# Revit family: Door-NanaWall-Acoustic-645_UPDATED_v2
name_source: partatom
category: Doors
units: mm (PartAtom-declared; Revit-internal decimal feet)

## family parameters
Always vertical = Yes
Cut with Voids When Loaded = No
Host = Wall
OmniClass Number = 23.30.10.17.17
OmniClass Title = Folding Doors and Grilles
Room Calculation Point = No
Shared = No

## types (3) — shared parameters
04 CSI = 08 41 13
95 CSI = 8411
Analytic Construction = <None>
Assembly Code = B2050.4010
Cost Info = https://www.nanawall.com
Description = Acoustical  floor supported folding glass wall
Disclaimer = Please note that the Revit model is for schematic purposes only.  To obtain a detailed 3D model, please go to the NanaWall's configurator at www.nanawall.com.
Engineering Details URL = https://www.nanawall.com
Filler = Rubber - NanaWall - Black
Glass Material = Glass - NanaWall - Generic
Installation and Service URL = http://www.nanawall.com
Keynote = 08 14 73
Manufacturer = NanaWall Systems, Inc.
Manufacturer Fax = (415) 383-0312
Model = NW Acoustical 645
Performance URL = https://www.nanawall.com
Product Page URL = https://www.nanawall.com
Sash = Metal - NanaWall - Aluminum
Sill = Metal - NanaWall - Aluminum
Sills Available = Flush Sill, Minimal Interior Sill
Subcategory = Folding Door
Thickness = 67.2 mm  [stored 0.220472 ft]
U Value = 0.27
URL = http://www.nanawall.com
Wall Closure = By host
Warranty URL = http://www.nanawall.com
c Hinge Offset = 33.6 mm
c Top Frame Lat Offset = 55.5 mm

## per-type parameters (varying)
| type | Constraints | c Down Offset |
| Standard | 3 | 2 mm  [stored 0.00656168 ft] |
| Flush Sill | 3 | 2 mm  [stored 0.00656168 ft] |
| Minimal Interior Sill | 4 | 0 mm  [stored 0 ft] |

note: [stored X ft] marks values corroborated as IEEE doubles in the binary element streams (Revit-internal decimal feet)

## geometry (parser evidence)
native form markers: Sweep x20
no freeform markers — native parametric forms only
